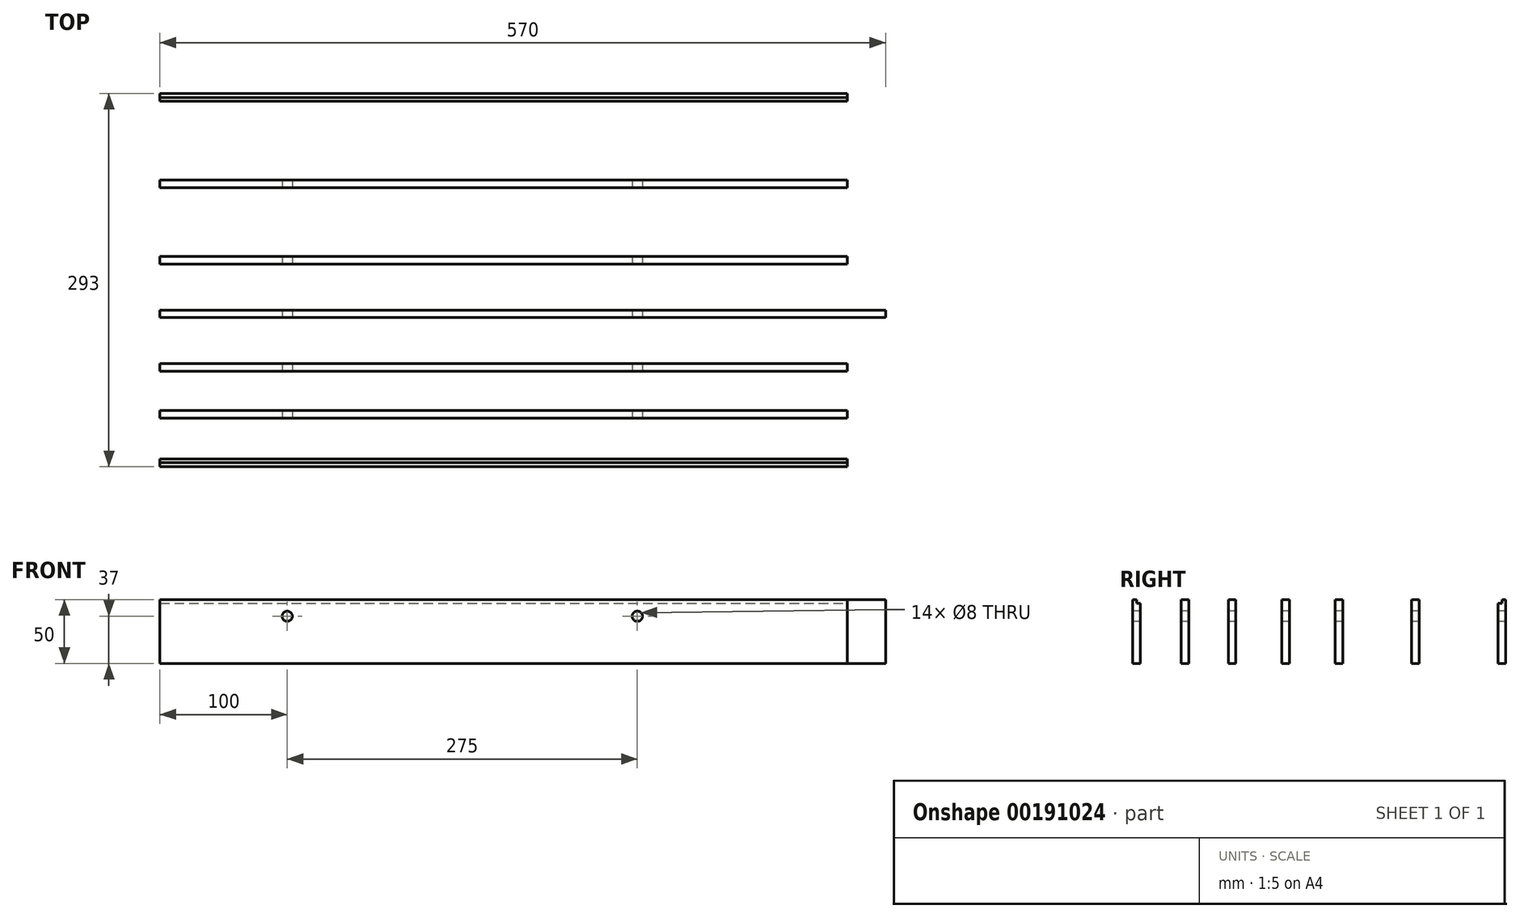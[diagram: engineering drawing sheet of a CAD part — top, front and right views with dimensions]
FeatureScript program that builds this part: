
annotation { "Feature Type Name" : "Feature", "Feature Type Description" : "" }
export const myFeature = defineFeature(function(context is Context, id is Id, definition is map)
    precondition{}
    {
        {
            var Q0;
            Q0=qCreatedBy(makeId("Front.planeOp"),FACE);
            var sketch = newSketch(context, id + "F0", { "sketchPlane" : qUnion([Q0])});
            skLineSegment(sketch, "E0.bottom", {"start": v(270, 25) * mm, "end": v(-270, 25) * mm});
            skLineSegment(sketch, "E0.top", {"start": v(270, -25) * mm, "end": v(-270, -25) * mm});
            skLineSegment(sketch, "E0.left", {"start": v(270, 25) * mm, "end": v(270, -25) * mm});
            skLineSegment(sketch, "E0.right", {"start": v(-270, 25) * mm, "end": v(-270, -25) * mm});
            skPoint(sketch, "E0.middle", {"position": v(0, 0) * mm});
            skSolve(sketch);
        }
        {
            var Q0;
            Q0=makeQuery(id+"F0.imprint","IMPRINT",FACE,{"disambiguationData":[TD([[makeQuery(id+"F0.imprint","IMPRINT",EDGE,{"derivedFrom":sQuery(id+"F0.wireOp",EDGE,"E0.bottom")}),1.0]])]});
            extrude(context, id + "F1", {"entities" : qUnion([Q0]), "depth" : 6 * mm});
        }
        {
            var Q0;
            Q0=makeQuery(id+"F1.opExtrude","CAP_FACE",FACE,{"disambiguationData":[OSD([sQuery(id+"F0.wireOp",EDGE,"E0.bottom"),sQuery(id+"F0.wireOp",EDGE,"E0.top"),sQuery(id+"F0.wireOp",EDGE,"E0.left"),sQuery(id+"F0.wireOp",EDGE,"E0.right")])],"isStart":false});
            var sketch = newSketch(context, id + "F2", { "sketchPlane" : qUnion([Q0])});
            skCircle(sketch, "E1", {"center": v(-170, 12) * mm, "radius": 4 * mm});
            skCircle(sketch, "E2", {"center": v(105, 12) * mm, "radius": 4 * mm});
            skSolve(sketch);
        }
        {
            var Q0;
            Q0=makeQuery(id+"F2.imprint","IMPRINT",FACE,{"disambiguationData":[TD([[makeQuery(id+"F2.imprint","IMPRINT",EDGE,{"derivedFrom":sQuery(id+"F2.wireOp",EDGE,"E1")}),1.0]])]});
            var Q1;
            Q1=makeQuery(id+"F2.imprint","IMPRINT",FACE,{"disambiguationData":[TD([[makeQuery(id+"F2.imprint","IMPRINT",EDGE,{"derivedFrom":sQuery(id+"F2.wireOp",EDGE,"E2")}),1.0]])]});
            var Q2;
            Q2=sQuery(id+"F2.wireOp",EDGE,"E1");
            var Q3;
            Q3=sQuery(id+"F2.wireOp",EDGE,"E2");
            extrude(context, id + "F3", {"entities" : qUnion([Q0, Q1]), "operationType" : NewBodyOperationType.REMOVE, "surfaceEntities" : qUnion([Q2, Q3]), "oppositeDirection" : true, "depth" : 25 * mm});
        }
        {
            var Q0;
            Q0=makeQuery(id+"F1.opExtrude","SWEPT_BODY",BODY,{"disambiguationData":[OSD([sQuery(id+"F0.wireOp",EDGE,"E0.bottom"),sQuery(id+"F0.wireOp",EDGE,"E0.top"),sQuery(id+"F0.wireOp",EDGE,"E0.left"),sQuery(id+"F0.wireOp",EDGE,"E0.right")])]});
            transform(context, id + "F4", {"entities" : qUnion([Q0]), "transformType" : TransformType.TRANSLATION_3D, "dx" : 0 * mm, "dy" : 38 * mm, "dz" : 0 * mm, "makeCopy" : true});
        }
        {
            var Q0;
            Q0=makeQuery(id+"F4.opPattern","COPY",BODY,{"derivedFrom":makeQuery(id+"F1.opExtrude","SWEPT_BODY",BODY,{"disambiguationData":[OSD([sQuery(id+"F0.wireOp",EDGE,"E0.bottom"),sQuery(id+"F0.wireOp",EDGE,"E0.top"),sQuery(id+"F0.wireOp",EDGE,"E0.left"),sQuery(id+"F0.wireOp",EDGE,"E0.right")])]}),"instanceName":"1"});
            transform(context, id + "F5", {"entities" : qUnion([Q0]), "transformType" : TransformType.TRANSLATION_3D, "dx" : 0 * mm, "dy" : 37 * mm, "dz" : 0 * mm, "makeCopy" : true});
        }
        {
            var Q0;
            Q0=makeQuery(id+"F5.opPattern","COPY",BODY,{"derivedFrom":makeQuery(id+"F4.opPattern","COPY",BODY,{"derivedFrom":makeQuery(id+"F1.opExtrude","SWEPT_BODY",BODY,{"disambiguationData":[OSD([sQuery(id+"F0.wireOp",EDGE,"E0.bottom"),sQuery(id+"F0.wireOp",EDGE,"E0.top"),sQuery(id+"F0.wireOp",EDGE,"E0.left"),sQuery(id+"F0.wireOp",EDGE,"E0.right")])]}),"instanceName":"1"}),"instanceName":"1"});
            transform(context, id + "F6", {"entities" : qUnion([Q0]), "transformType" : TransformType.TRANSLATION_3D, "dx" : 0 * mm, "dy" : 42 * mm, "dz" : 0 * mm, "makeCopy" : true});
        }
        {
            var Q0;
            Q0=makeQuery(id+"F6.opPattern","COPY",BODY,{"derivedFrom":makeQuery(id+"F5.opPattern","COPY",BODY,{"derivedFrom":makeQuery(id+"F4.opPattern","COPY",BODY,{"derivedFrom":makeQuery(id+"F1.opExtrude","SWEPT_BODY",BODY,{"disambiguationData":[OSD([sQuery(id+"F0.wireOp",EDGE,"E0.bottom"),sQuery(id+"F0.wireOp",EDGE,"E0.top"),sQuery(id+"F0.wireOp",EDGE,"E0.left"),sQuery(id+"F0.wireOp",EDGE,"E0.right")])]}),"instanceName":"1"}),"instanceName":"1"}),"instanceName":"1"});
            transform(context, id + "F7", {"entities" : qUnion([Q0]), "transformType" : TransformType.TRANSLATION_3D, "dx" : 0 * mm, "dy" : 42 * mm, "dz" : 0 * mm, "makeCopy" : true});
        }
        {
            var Q0;
            Q0=makeQuery(id+"F7.opPattern","COPY",BODY,{"derivedFrom":makeQuery(id+"F6.opPattern","COPY",BODY,{"derivedFrom":makeQuery(id+"F5.opPattern","COPY",BODY,{"derivedFrom":makeQuery(id+"F4.opPattern","COPY",BODY,{"derivedFrom":makeQuery(id+"F1.opExtrude","SWEPT_BODY",BODY,{"disambiguationData":[OSD([sQuery(id+"F0.wireOp",EDGE,"E0.bottom"),sQuery(id+"F0.wireOp",EDGE,"E0.top"),sQuery(id+"F0.wireOp",EDGE,"E0.left"),sQuery(id+"F0.wireOp",EDGE,"E0.right")])]}),"instanceName":"1"}),"instanceName":"1"}),"instanceName":"1"}),"instanceName":"1"});
            transform(context, id + "F8", {"entities" : qUnion([Q0]), "transformType" : TransformType.TRANSLATION_3D, "dx" : 0 * mm, "dy" : 60 * mm, "dz" : 0 * mm, "makeCopy" : true});
        }
        {
            var Q0;
            Q0=makeQuery(id+"F8.opPattern","COPY",BODY,{"derivedFrom":makeQuery(id+"F7.opPattern","COPY",BODY,{"derivedFrom":makeQuery(id+"F6.opPattern","COPY",BODY,{"derivedFrom":makeQuery(id+"F5.opPattern","COPY",BODY,{"derivedFrom":makeQuery(id+"F4.opPattern","COPY",BODY,{"derivedFrom":makeQuery(id+"F1.opExtrude","SWEPT_BODY",BODY,{"disambiguationData":[OSD([sQuery(id+"F0.wireOp",EDGE,"E0.bottom"),sQuery(id+"F0.wireOp",EDGE,"E0.top"),sQuery(id+"F0.wireOp",EDGE,"E0.left"),sQuery(id+"F0.wireOp",EDGE,"E0.right")])]}),"instanceName":"1"}),"instanceName":"1"}),"instanceName":"1"}),"instanceName":"1"}),"instanceName":"1"});
            transform(context, id + "F9", {"entities" : qUnion([Q0]), "transformType" : TransformType.TRANSLATION_3D, "dx" : 0 * mm, "dy" : 68 * mm, "dz" : 0 * mm, "makeCopy" : true});
        }
        {
            var Q0;
            Q0=makeQuery(id+"F6.opPattern","COPY",FACE,{"derivedFrom":makeQuery(id+"F5.opPattern","COPY",FACE,{"derivedFrom":makeQuery(id+"F4.opPattern","COPY",FACE,{"derivedFrom":makeQuery(id+"F1.opExtrude","SWEPT_FACE",FACE,{"disambiguationData":[OSD([sQuery(id+"F0.wireOp",EDGE,"E0.left")])]}),"instanceName":"1"}),"instanceName":"1"}),"instanceName":"1"});
            extrude(context, id + "F10", {"entities" : qUnion([Q0]), "operationType" : NewBodyOperationType.ADD, "depth" : 30 * mm});
        }
        {
            var Q0;
            Q0=makeQuery(id+"F9.opPattern","COPY",FACE,{"derivedFrom":makeQuery(id+"F8.opPattern","COPY",FACE,{"derivedFrom":makeQuery(id+"F7.opPattern","COPY",FACE,{"derivedFrom":makeQuery(id+"F6.opPattern","COPY",FACE,{"derivedFrom":makeQuery(id+"F5.opPattern","COPY",FACE,{"derivedFrom":makeQuery(id+"F4.opPattern","COPY",FACE,{"derivedFrom":makeQuery(id+"F1.opExtrude","SWEPT_FACE",FACE,{"disambiguationData":[OSD([sQuery(id+"F0.wireOp",EDGE,"E0.left")])]}),"instanceName":"1"}),"instanceName":"1"}),"instanceName":"1"}),"instanceName":"1"}),"instanceName":"1"}),"instanceName":"1"});
            var sketch = newSketch(context, id + "F11", { "sketchPlane" : qUnion([Q0])});
            skPoint(sketch, "E3.oppositeSnap0", {"position": v(284, 25) * mm});
            skLineSegment(sketch, "E3.bottom", {"start": v(281, 25) * mm, "end": v(284, 25) * mm});
            skLineSegment(sketch, "E3.top", {"start": v(281, 22) * mm, "end": v(284, 22) * mm});
            skLineSegment(sketch, "E3.left", {"start": v(281, 25) * mm, "end": v(281, 22) * mm});
            skLineSegment(sketch, "E3.right", {"start": v(284, 25) * mm, "end": v(284, 22) * mm});
            skSolve(sketch);
        }
        {
            var Q0;
            Q0=makeQuery(id+"F11.imprint","IMPRINT",FACE,{"disambiguationData":[TD([[makeQuery(id+"F11.imprint","IMPRINT",EDGE,{"derivedFrom":sQuery(id+"F11.wireOp",EDGE,"E3.bottom")}),-1.0]])]});
            extrude(context, id + "F12", {"entities" : qUnion([Q0]), "operationType" : NewBodyOperationType.REMOVE, "oppositeDirection" : true, "depth" : 560 * mm});
        }
        {
            var Q0;
            Q0=makeQuery(id+"F1.opExtrude","SWEPT_FACE",FACE,{"disambiguationData":[OSD([sQuery(id+"F0.wireOp",EDGE,"E0.left")])]});
            var sketch = newSketch(context, id + "F13", { "sketchPlane" : qUnion([Q0])});
            skLineSegment(sketch, "E4.bottom", {"start": v(0, 25) * mm, "end": v(-3, 25) * mm});
            skLineSegment(sketch, "E4.top", {"start": v(0, 22) * mm, "end": v(-3, 22) * mm});
            skLineSegment(sketch, "E4.left", {"start": v(0, 25) * mm, "end": v(0, 22) * mm});
            skLineSegment(sketch, "E4.right", {"start": v(-3, 25) * mm, "end": v(-3, 22) * mm});
            skSolve(sketch);
        }
        {
            var Q0;
            Q0=makeQuery(id+"F13.imprint","IMPRINT",FACE,{"disambiguationData":[TD([[makeQuery(id+"F13.imprint","IMPRINT",EDGE,{"derivedFrom":sQuery(id+"F13.wireOp",EDGE,"E4.bottom")}),-1.0]])]});
            extrude(context, id + "F14", {"entities" : qUnion([Q0]), "operationType" : NewBodyOperationType.REMOVE, "oppositeDirection" : true, "depth" : 560 * mm});
        }
    });
